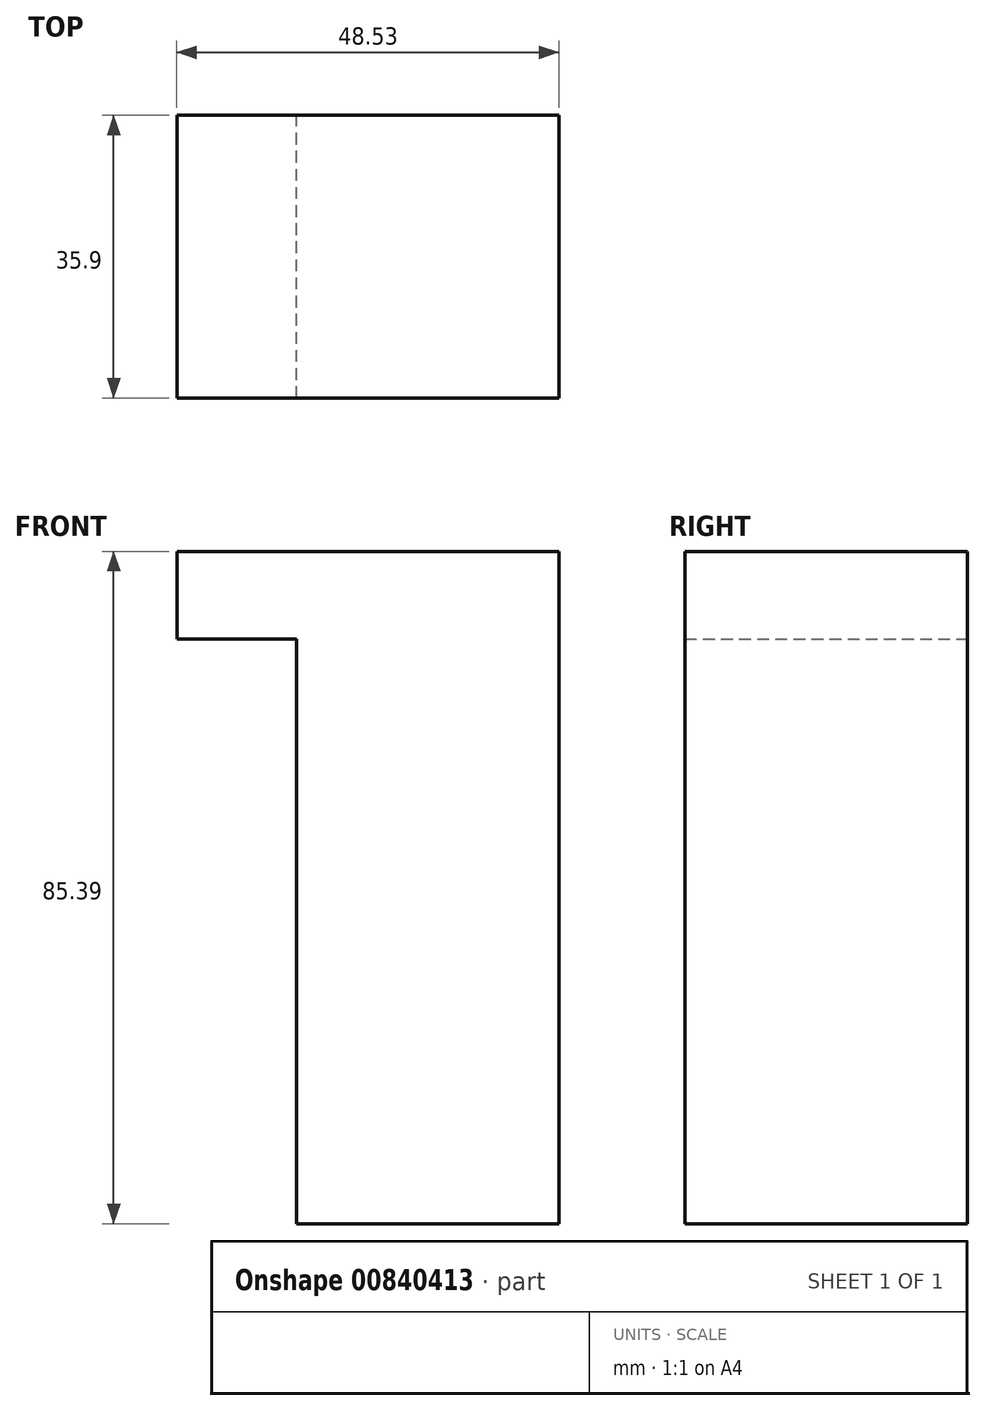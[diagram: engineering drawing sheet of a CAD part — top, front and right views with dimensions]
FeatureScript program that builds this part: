
annotation { "Feature Type Name" : "Feature", "Feature Type Description" : "" }
export const myFeature = defineFeature(function(context is Context, id is Id, definition is map)
    precondition{}
    {
        {
            var Q0;
            Q0=qCreatedBy(makeId("Front.planeOp"),FACE);
            var sketch = newSketch(context, id + "F0", { "sketchPlane" : qUnion([Q0])});
            skLineSegment(sketch, "E0.bottom", {"start": v(25.4, 24.3) * mm, "end": v(40.62, 24.3) * mm});
            skLineSegment(sketch, "E0.top", {"start": v(25.4, 35.44) * mm, "end": v(73.92, 35.44) * mm});
            skLineSegment(sketch, "E0.left", {"start": v(25.4, 24.3) * mm, "end": v(25.4, 35.44) * mm});
            skLineSegment(sketch, "E0.right", {"start": v(73.92, 24.3) * mm, "end": v(73.92, 35.44) * mm});
            skLineSegment(sketch, "E1.top", {"start": v(73.92, -49.95) * mm, "end": v(40.62, -49.95) * mm});
            skLineSegment(sketch, "E1.left", {"start": v(73.92, 24.3) * mm, "end": v(73.92, -49.95) * mm});
            skLineSegment(sketch, "E1.right", {"start": v(40.62, 24.3) * mm, "end": v(40.62, -49.95) * mm});
            skSolve(sketch);
        }
        {
            var Q0;
            Q0 = qSketchRegion(id + "F0", true);
            extrude(context, id + "F1", {"entities" : qUnion([Q0]), "depth" : 35.9 * mm, "offsetDistance" : 25.4 * mm});
        }
    });
